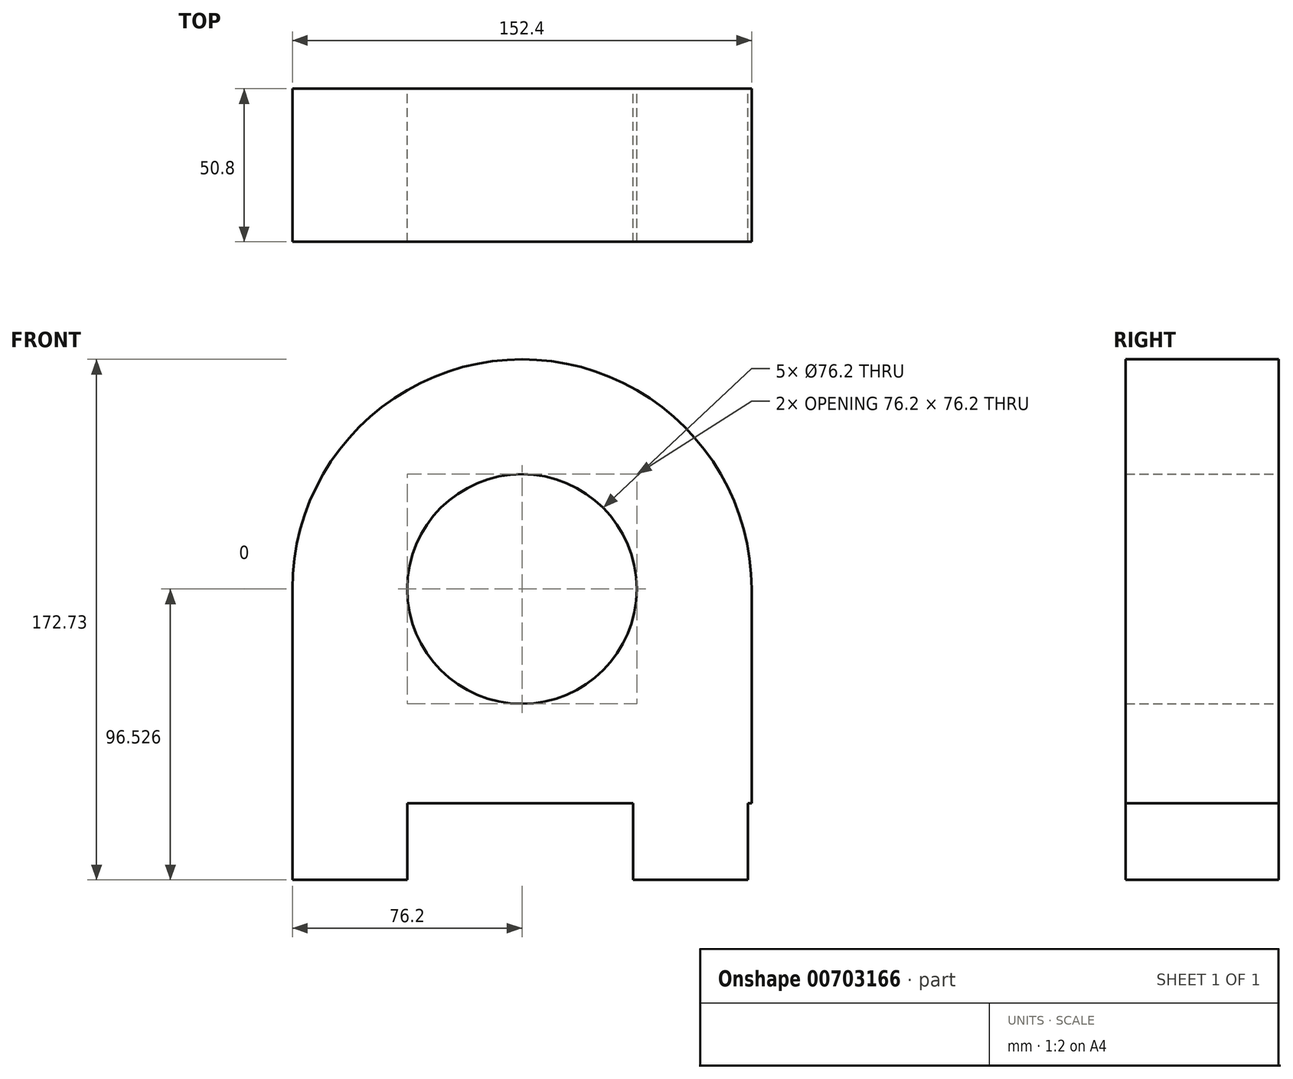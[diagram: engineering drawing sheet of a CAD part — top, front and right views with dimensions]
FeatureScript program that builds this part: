
annotation { "Feature Type Name" : "Feature", "Feature Type Description" : "" }
export const myFeature = defineFeature(function(context is Context, id is Id, definition is map)
    precondition{}
    {
        {
            var Q0;
            Q0=qCreatedBy(makeId("Front.planeOp"),FACE);
            var sketch = newSketch(context, id + "F0", { "sketchPlane" : qUnion([Q0])});
            skLineSegment(sketch, "E0.bottom", {"start": v(-77.5, -24) * mm, "end": v(-39.4, -24) * mm});
            skLineSegment(sketch, "E0.top", {"start": v(-77.5, -49.4) * mm, "end": v(-39.4, -49.4) * mm});
            skLineSegment(sketch, "E0.left", {"start": v(-77.5, -24) * mm, "end": v(-77.5, -49.4) * mm});
            skLineSegment(sketch, "E0.right", {"start": v(-39.4, -24) * mm, "end": v(-39.4, -49.4) * mm});
            skLineSegment(sketch, "E1", {"start": v(-39.4, -24) * mm, "end": v(35.56, -24) * mm});
            skLineSegment(sketch, "E2.bottom", {"start": v(35.56, -24) * mm, "end": v(73.66, -24) * mm});
            skLineSegment(sketch, "E2.top", {"start": v(35.56, -49.4) * mm, "end": v(73.66, -49.4) * mm});
            skLineSegment(sketch, "E2.left", {"start": v(35.56, -24) * mm, "end": v(35.56, -49.4) * mm});
            skLineSegment(sketch, "E2.right", {"start": v(73.66, -24) * mm, "end": v(73.66, -49.4) * mm});
            skLineSegment(sketch, "E3.bottom", {"start": v(-77.5, -24) * mm, "end": v(0.98, -24) * mm});
            skLineSegment(sketch, "E4.bottom", {"start": v(-77.5, -24) * mm, "end": v(74.9, -24) * mm});
            skLineSegment(sketch, "E4.top", {"start": v(-77.5, 47.13) * mm, "end": v(74.9, 47.13) * mm});
            skLineSegment(sketch, "E4.left", {"start": v(-77.5, -24) * mm, "end": v(-77.5, 47.13) * mm});
            skLineSegment(sketch, "E4.right", {"start": v(74.9, -24) * mm, "end": v(74.9, 47.13) * mm});
            skArc(sketch, "E5", {"start": v(74.9, 47.13) * mm, "mid": v(-1.3, 123.34) * mm, "end": v(-77.5, 47.13) * mm});
            skLineSegment(sketch, "E6", {"start": v(0, 123.33) * mm, "end": v(0, 47.13) * mm});
            skSolve(sketch);
        }
        {
            var Q0;
            Q0 = qSketchRegion(id + "F0", true);
            extrude(context, id + "F1", {"entities" : qUnion([Q0]), "depth" : 50.8 * mm, "offsetDistance" : 25.4 * mm});
        }
        {
            var Q0;
            Q0=sQuery(id+"F0.wireOp",VERTEX,"E5.center");
            var Q1;
            Q1=makeQuery(id+"F1.opExtrude","SWEPT_BODY",BODY,{"disambiguationData":[OSD([sQuery(id+"F0.wireOp",EDGE,"E0.top"),sQuery(id+"F0.wireOp",EDGE,"E0.left"),sQuery(id+"F0.wireOp",EDGE,"E0.right"),sQuery(id+"F0.wireOp",EDGE,"E2.top"),sQuery(id+"F0.wireOp",EDGE,"E2.left"),sQuery(id+"F0.wireOp",EDGE,"E2.right"),sQuery(id+"F0.wireOp",EDGE,"E4.bottom"),sQuery(id+"F0.wireOp",EDGE,"E4.left"),sQuery(id+"F0.wireOp",EDGE,"E4.right"),sQuery(id+"F0.wireOp",EDGE,"E5")])]});
            hole(context, id + "F2", {"style" : HoleStyle.SIMPLE, "endStyle" : HoleEndStyle.THROUGH, "oppositeDirection" : true, "holeDiameter" : 76.2 * mm, "majorDiameter" : 6.35 * mm, "isTappedThrough" : true, "tappedDepth" : 12.7 * mm, "tapClearance" : 3, "locations" : qUnion([Q0]), "scope" : qUnion([Q1])});
        }
    });
